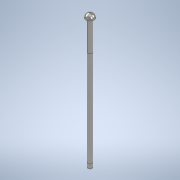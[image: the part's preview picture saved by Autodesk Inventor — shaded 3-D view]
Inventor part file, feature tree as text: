
AUTODESK INVENTOR PART (.ipt)
format: ipt  version: 2021 (Build 250183000, 183)  size: 147,456 bytes
history: native  units: mm
features: sketch x5, split x3, extrude x2, fillet x1
ambient origin geometry x8: Origin, YZ Plane, XZ Plane, XY Plane, X Axis, Y Axis, Z Axis, Center Point
bodies: Solid1 (feature_tree)
feature tree (11):
  extrude  "Extrusion1"  Depth=610.0mm TaperAngle=0.0deg
  extrude  "Extrusion2"  Depth=20.0mm TaperAngle=0.0deg
  fillet  "Fillet1"  Radius=20.0mm
  split  "Split1"
  split  "Split2"
  split  "Split3"
  sketch  "Sketch1"  dims[d0=20.0mm d1=610.0mm d2=0.0mm]
  sketch  "Sketch2"  dims[d3=40.0mm d4=20.0mm d5=0.0mm d6=20.0mm]
  sketch  "Sketch3"
  sketch  "Sketch4"
  sketch  "Sketch5"
